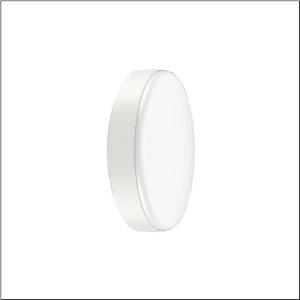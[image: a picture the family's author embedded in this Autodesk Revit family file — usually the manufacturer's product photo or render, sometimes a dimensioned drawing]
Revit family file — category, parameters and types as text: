
# Revit family: rondel_31_51wc10mb34a
name_source: partatom
category: Lighting Fixtures
units: mm (PartAtom-declared; Revit-internal decimal feet)

## family parameters
Cut with Voids When Loaded = No
Host = Face
Light Source = No
Part Type = Normal
Room Calculation Point = No
Round Connector Dimension = Use Diameter
Shared = No

## types (1)
- --- (1 x LED, 4250 lm, 34 W, 3000K)
    Apparent Load = 34 VA
    CIE Flux Codes = 44 75 94 94 100
    Color Rendering = 80
    Color Temperature = 3000K
    Default Elevation = 1800 mm
    Description = Rondel 31, wall and ceiling luminaire, primary optical cover: cover, of PC, opal, light emission: direct distribution, primary light characteristic: symmetric, installation type: surface-mounted, LED, rated luminous flux: 4.250lm, luminous efficacy: 125lm/W, light colour: 830, colour temperature: 3000K, with terminal, 3-pole, max. 2.5mm², mains connection: 220..240V, AC, 50/60Hz, rated input power: 34W, luminaire housing, of PC, traffic white (RAL 9016), diameter: 480mm, protection rating (complete): IP65, insulation class (complete): insulation class II (safety insulation), certification: CE, impact resistance: IK10, permissible operating ambient temperature: -20..+40°C, permissible storage temperature: -20..+60°C, packaging unit: 1 piece
    Height = 97 mm
    Lamp = 1 x LED
    Lamp Light Flux = 4250 lm
    Lamp Power = 34 W
    Lamp count = 1
    Length = 480 mm
    Luminous efficacy = 125 lm/W
    Manufacturer = Siteco
    ModVariant = No
    Model = 51WC10MB34A
    Mounting Place = Ceiling
    Mounting Type = Surface mounted
    Number of Poles = 1
    OnlyDefault = Yes
    Power Factor = 1
    Product Name = Rondel 31
    Product group = wall and ceiling luminaire
    ProductGroupID = 301
    Protection Class = Protection class II
    Protection Degree = IP 65
    RLX_Detail_Level = 1
    RLX_Emergency_Light_Flux = 0 lm
    RLX_Emergency_Type = 0
    RLX_Emergency_Type_DB = No
    RlxData = <blob elided: 41237 chars, md5=16ac7bfd>
    Socket = socket
    Standby Power = 0 W
    System Light Flux = 4250 lm
    System Power = 34 W
    Type Comments = factory setting: luminous flux: 100 % | (ON | ON)
    Type Image = l_1007188.jpg
    URL = http://relux.com
    VarID = @adj_083043
    Voltage = 0 V
    Weight = 0.00 kg
    Width = 0 mm  [stored 0 ft]

note: [stored X ft] marks values corroborated as IEEE doubles in the binary element streams (Revit-internal decimal feet)

## geometry (parser evidence)
native form markers: Blend x4, Sweep x11
no freeform markers — native parametric forms only
